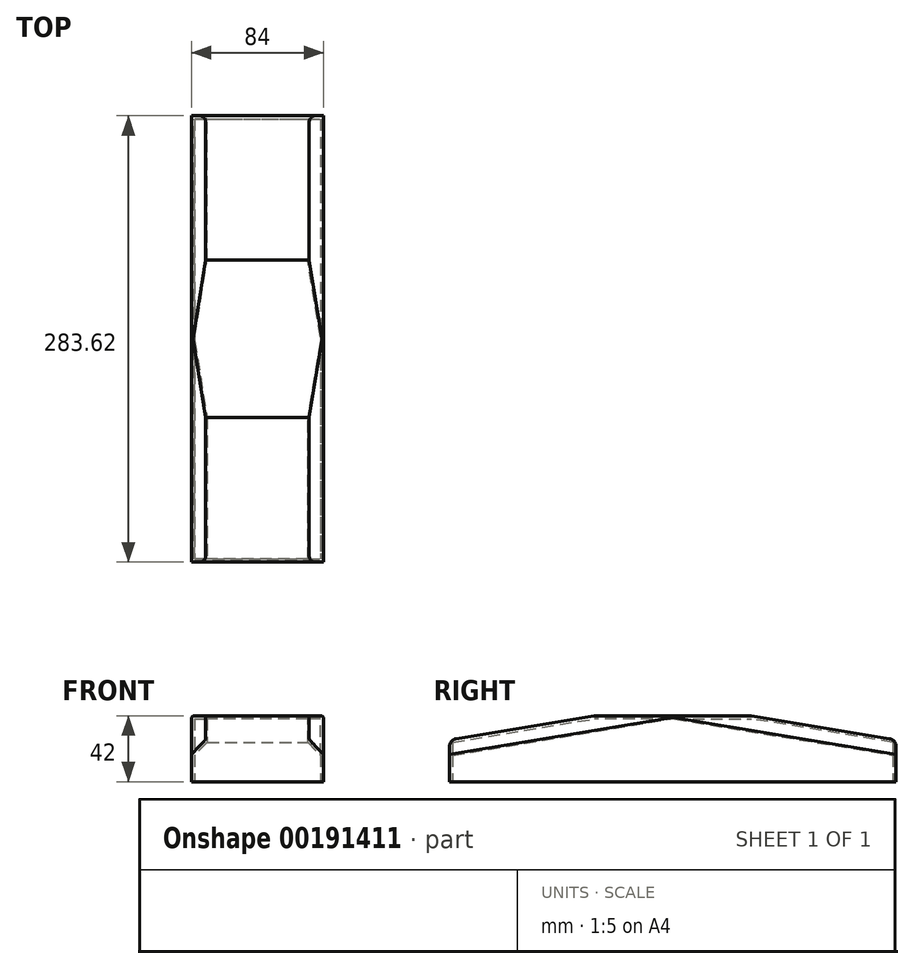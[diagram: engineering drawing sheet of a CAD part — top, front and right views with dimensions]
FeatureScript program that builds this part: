
annotation { "Feature Type Name" : "Feature", "Feature Type Description" : "" }
export const myFeature = defineFeature(function(context is Context, id is Id, definition is map)
    precondition{}
    {
        {
            var Q0;
            Q0=qCreatedBy(makeId("Top.planeOp"),FACE);
            var sketch = newSketch(context, id + "F0", { "sketchPlane" : qUnion([Q0])});
            skLineSegment(sketch, "E0.bottom", {"start": v(-40, 139.8) * mm, "end": v(40, 139.8) * mm});
            skLineSegment(sketch, "E0.top", {"start": v(-40, -139.8) * mm, "end": v(40, -139.8) * mm});
            skLineSegment(sketch, "E0.left", {"start": v(-40, 139.8) * mm, "end": v(-40, -139.8) * mm});
            skLineSegment(sketch, "E0.right", {"start": v(40, 139.8) * mm, "end": v(40, -139.8) * mm});
            skSolve(sketch);
        }
        {
            var Q0;
            Q0=makeQuery(id+"F0.imprint","IMPRINT",FACE,{"disambiguationData":[TD([[makeQuery(id+"F0.imprint","IMPRINT",EDGE,{"derivedFrom":sQuery(id+"F0.wireOp",EDGE,"E0.bottom")}),-1.0]])]});
            extrude(context, id + "F1", {"entities" : qUnion([Q0]), "depth" : 40 * mm});
        }
        {
            var Q0;
            Q0=makeQuery(id+"F1.opExtrude","CAP_EDGE",EDGE,{"disambiguationData":[OSD([sQuery(id+"F0.wireOp",EDGE,"E0.bottom")])],"isStart":false});
            var Q1;
            Q1=makeQuery(id+"F1.opExtrude","CAP_EDGE",EDGE,{"disambiguationData":[OSD([sQuery(id+"F0.wireOp",EDGE,"E0.top")])],"isStart":false});
            chamfer(context, id + "F2", {"entities" : qUnion([Q0, Q1]), "chamferType" : ChamferType.TWO_OFFSETS, "width1" : 15 * mm, "oppositeDirection" : false, "width2" : 90 * mm});
        }
        {
            var Q0;
            Q0=makeQuery(id+"F2.opChamfer","BLEND_EDGE",EDGE,{"blendedFrom":[makeQuery(id+"F1.opExtrude","CAP_EDGE",EDGE,{"disambiguationData":[OSD([sQuery(id+"F0.wireOp",EDGE,"E0.top")])],"isStart":false}),makeQuery(id+"F1.opExtrude","SWEPT_FACE",FACE,{"disambiguationData":[OSD([sQuery(id+"F0.wireOp",EDGE,"E0.left")])]})],"blendedInto":[makeQuery(id+"F1.opExtrude","SWEPT_FACE",FACE,{"disambiguationData":[OSD([sQuery(id+"F0.wireOp",EDGE,"E0.left")])]})]});
            var Q1;
            Q1=makeQuery(id+"F2.opChamfer","BLEND_EDGE",EDGE,{"blendedFrom":[makeQuery(id+"F1.opExtrude","CAP_EDGE",EDGE,{"disambiguationData":[OSD([sQuery(id+"F0.wireOp",EDGE,"E0.top")])],"isStart":false}),makeQuery(id+"F1.opExtrude","SWEPT_FACE",FACE,{"disambiguationData":[OSD([sQuery(id+"F0.wireOp",EDGE,"E0.right")])]})],"blendedInto":[makeQuery(id+"F1.opExtrude","SWEPT_FACE",FACE,{"disambiguationData":[OSD([sQuery(id+"F0.wireOp",EDGE,"E0.right")])]})]});
            var Q2;
            Q2=makeQuery(id+"F2.opChamfer","BLEND_EDGE",EDGE,{"blendedFrom":[makeQuery(id+"F1.opExtrude","CAP_EDGE",EDGE,{"disambiguationData":[OSD([sQuery(id+"F0.wireOp",EDGE,"E0.bottom")])],"isStart":false}),makeQuery(id+"F1.opExtrude","SWEPT_FACE",FACE,{"disambiguationData":[OSD([sQuery(id+"F0.wireOp",EDGE,"E0.right")])]})],"blendedInto":[makeQuery(id+"F1.opExtrude","SWEPT_FACE",FACE,{"disambiguationData":[OSD([sQuery(id+"F0.wireOp",EDGE,"E0.right")])]})]});
            var Q3;
            Q3=makeQuery(id+"F2.opChamfer","BLEND_EDGE",EDGE,{"blendedFrom":[makeQuery(id+"F1.opExtrude","CAP_EDGE",EDGE,{"disambiguationData":[OSD([sQuery(id+"F0.wireOp",EDGE,"E0.bottom")])],"isStart":false}),makeQuery(id+"F1.opExtrude","SWEPT_FACE",FACE,{"disambiguationData":[OSD([sQuery(id+"F0.wireOp",EDGE,"E0.left")])]})],"blendedInto":[makeQuery(id+"F1.opExtrude","SWEPT_FACE",FACE,{"disambiguationData":[OSD([sQuery(id+"F0.wireOp",EDGE,"E0.left")])]})]});
            chamfer(context, id + "F3", {"entities" : qUnion([Q0, Q1, Q2, Q3]), "width" : 8 * mm, "tangentPropagation" : true});
        }
        {
            var Q0;
            Q0=makeQuery(id+"F1.opExtrude","CAP_FACE",FACE,{"disambiguationData":[OSD([sQuery(id+"F0.wireOp",EDGE,"E0.bottom"),sQuery(id+"F0.wireOp",EDGE,"E0.top"),sQuery(id+"F0.wireOp",EDGE,"E0.left"),sQuery(id+"F0.wireOp",EDGE,"E0.right")])],"isStart":true});
            shell(context, id + "F4", {"entities" : qUnion([Q0]), "thickness" : 2 * mm, "oppositeDirection" : true});
        }
        {
            var Q0;
            {var subQ0=sQuery(id+"F0.wireOp",EDGE,"E0.top");Q0=makeQuery(id+"F2.opChamfer","BLEND_EDGE",EDGE,{"blendedFrom":[makeQuery(id+"F1.opExtrude","CAP_EDGE",EDGE,{"disambiguationData":[OSD([subQ0])],"isStart":false}),makeQuery(id+"F1.opExtrude","SWEPT_FACE",FACE,{"disambiguationData":[OSD([subQ0])]})],"blendedInto":[makeQuery(id+"F1.opExtrude","SWEPT_FACE",FACE,{"disambiguationData":[OSD([subQ0])]})]});}
            var Q1;
            {var subQ0=sQuery(id+"F0.wireOp",EDGE,"E0.bottom");Q1=makeQuery(id+"F2.opChamfer","BLEND_EDGE",EDGE,{"blendedFrom":[makeQuery(id+"F1.opExtrude","CAP_EDGE",EDGE,{"disambiguationData":[OSD([subQ0])],"isStart":false}),makeQuery(id+"F1.opExtrude","SWEPT_FACE",FACE,{"disambiguationData":[OSD([subQ0])]})],"blendedInto":[makeQuery(id+"F1.opExtrude","SWEPT_FACE",FACE,{"disambiguationData":[OSD([subQ0])]})]});}
            fillet(context, id + "F5", {"entities" : qUnion([Q0, Q1]), "radius" : 5 * mm, "tangentPropagation" : true, "allowEdgeOverflow" : false});
        }
    });
